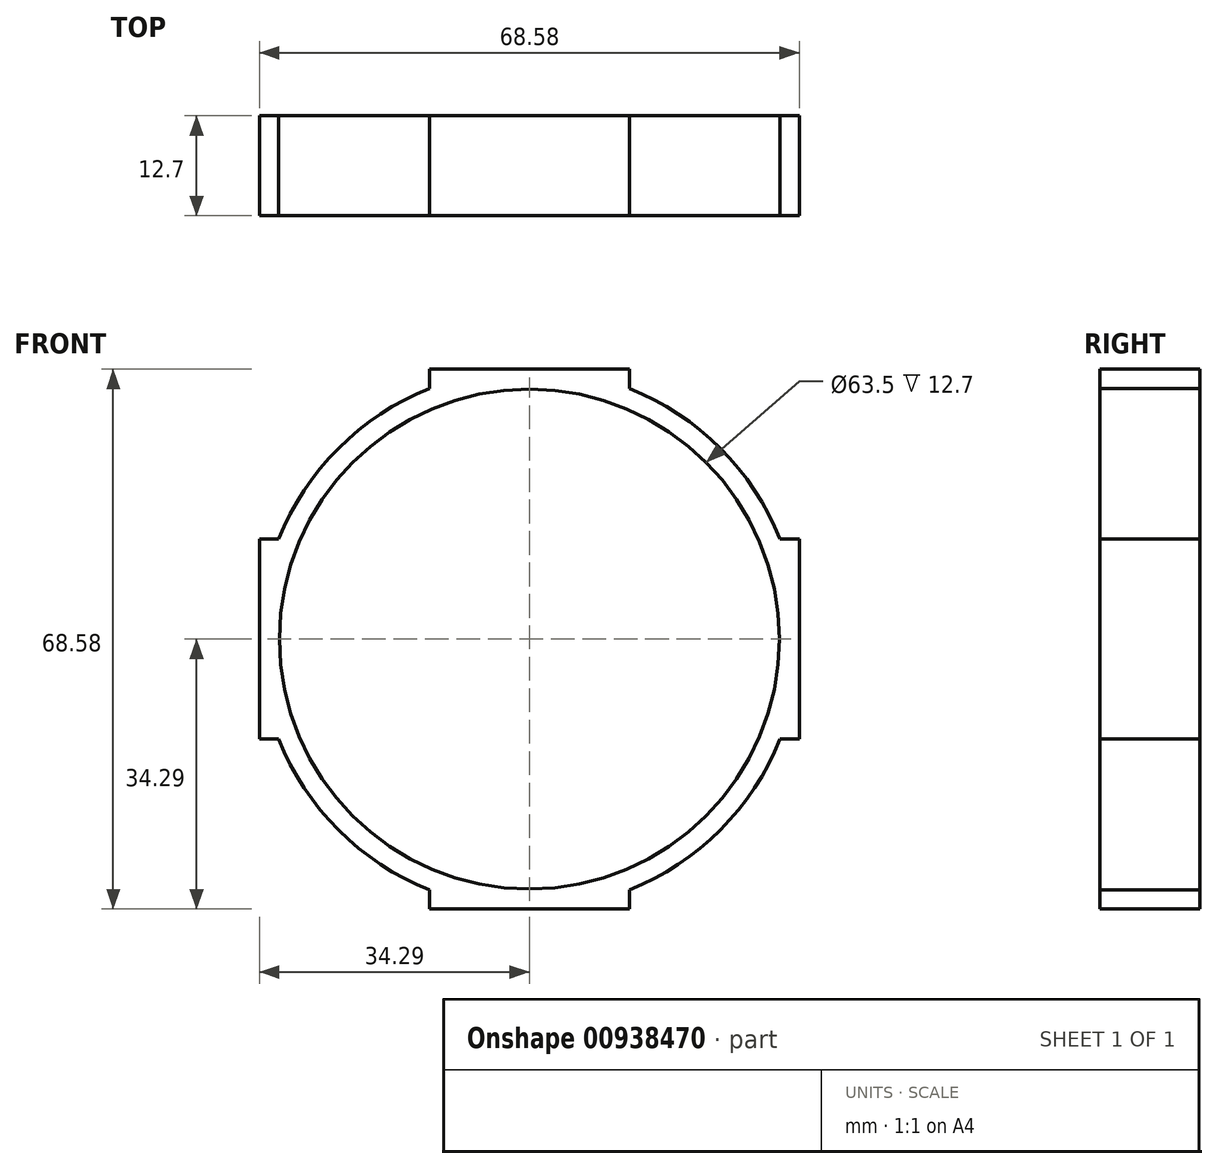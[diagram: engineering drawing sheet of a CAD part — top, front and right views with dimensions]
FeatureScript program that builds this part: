
annotation { "Feature Type Name" : "Feature", "Feature Type Description" : "" }
export const myFeature = defineFeature(function(context is Context, id is Id, definition is map)
    precondition{}
    {
        {
            var Q0;
            Q0=qCreatedBy(makeId("Front.planeOp"),FACE);
            var sketch = newSketch(context, id + "F0", { "sketchPlane" : qUnion([Q0])});
            skCircle(sketch, "E0", {"center": v(0, 0) * mm, "radius": 34.3 * mm});
            skCircle(sketch, "E1", {"center": v(0, 0) * mm, "radius": 31.75 * mm});
            skLineSegment(sketch, "E2", {"start": v(-12.7, 34.3) * mm, "end": v(12.7, 34.3) * mm});
            skLineSegment(sketch, "E3", {"start": v(12.7, 34.3) * mm, "end": v(12.7, 31.85) * mm});
            skLineSegment(sketch, "E4", {"start": v(-12.7, 34.3) * mm, "end": v(-12.7, 31.85) * mm});
            skLineSegment(sketch, "E5.MirrorCS", {"start": v(12.7, -34.3) * mm, "end": v(12.7, -31.85) * mm});
            skLineSegment(sketch, "E6.MirrorCS", {"start": v(-12.7, -34.3) * mm, "end": v(12.7, -34.3) * mm});
            skLineSegment(sketch, "E7.MirrorCS", {"start": v(-12.7, -34.3) * mm, "end": v(-12.7, -31.85) * mm});
            skLineSegment(sketch, "E8", {"start": v(-31.85, -12.7) * mm, "end": v(-34.3, -12.7) * mm});
            skLineSegment(sketch, "E9", {"start": v(-34.3, -12.7) * mm, "end": v(-34.3, 12.7) * mm});
            skLineSegment(sketch, "E10", {"start": v(-34.3, 12.7) * mm, "end": v(-31.85, 12.7) * mm});
            skLineSegment(sketch, "E11.MirrorCS", {"start": v(34.3, 12.7) * mm, "end": v(31.85, 12.7) * mm});
            skLineSegment(sketch, "E12.MirrorCS", {"start": v(34.3, -12.7) * mm, "end": v(34.3, 12.7) * mm});
            skLineSegment(sketch, "E13.MirrorCS", {"start": v(31.85, -12.7) * mm, "end": v(34.3, -12.7) * mm});
            skSolve(sketch);
        }
        {
            var Q0;
            Q0=makeQuery(id+"F0.imprint","IMPRINT",FACE,{"disambiguationData":[TD([[makeQuery(id+"F0.imprint","IMPRINT",EDGE,{"derivedFrom":sQuery(id+"F0.wireOp",EDGE,"E0")}),1.0]])]});
            var Q1;
            {var subQ0=sQuery(id+"F0.wireOp",EDGE,"E10");Q1=makeQuery(id+"F0.imprint","IMPRINT",FACE,{"disambiguationData":[TD([[makeQuery(id+"F0.imprint","IMPRINT",EDGE,{"derivedFrom":subQ0}),-1.0]])]});}
            var Q2;
            {var subQ0=sQuery(id+"F0.wireOp",EDGE,"E8");Q2=makeQuery(id+"F0.imprint","IMPRINT",FACE,{"disambiguationData":[TD([[makeQuery(id+"F0.imprint","IMPRINT",EDGE,{"derivedFrom":subQ0}),-1.0]])]});}
            var Q3;
            {var subQ0=sQuery(id+"F0.wireOp",EDGE,"E4");Q3=makeQuery(id+"F0.imprint","IMPRINT",FACE,{"disambiguationData":[TD([[makeQuery(id+"F0.imprint","IMPRINT",EDGE,{"derivedFrom":subQ0}),1.0]])]});}
            var Q4;
            {var subQ0=sQuery(id+"F0.wireOp",EDGE,"E3");Q4=makeQuery(id+"F0.imprint","IMPRINT",FACE,{"disambiguationData":[TD([[makeQuery(id+"F0.imprint","IMPRINT",EDGE,{"derivedFrom":subQ0}),-1.0]])]});}
            var Q5;
            {var subQ0=sQuery(id+"F0.wireOp",EDGE,"E11.MirrorCS");Q5=makeQuery(id+"F0.imprint","IMPRINT",FACE,{"disambiguationData":[TD([[makeQuery(id+"F0.imprint","IMPRINT",EDGE,{"derivedFrom":subQ0}),1.0]])]});}
            var Q6;
            {var subQ0=sQuery(id+"F0.wireOp",EDGE,"E13.MirrorCS");Q6=makeQuery(id+"F0.imprint","IMPRINT",FACE,{"disambiguationData":[TD([[makeQuery(id+"F0.imprint","IMPRINT",EDGE,{"derivedFrom":subQ0}),1.0]])]});}
            var Q7;
            {var subQ0=sQuery(id+"F0.wireOp",EDGE,"E5.MirrorCS");Q7=makeQuery(id+"F0.imprint","IMPRINT",FACE,{"disambiguationData":[TD([[makeQuery(id+"F0.imprint","IMPRINT",EDGE,{"derivedFrom":subQ0}),1.0]])]});}
            var Q8;
            {var subQ0=sQuery(id+"F0.wireOp",EDGE,"E7.MirrorCS");Q8=makeQuery(id+"F0.imprint","IMPRINT",FACE,{"disambiguationData":[TD([[makeQuery(id+"F0.imprint","IMPRINT",EDGE,{"derivedFrom":subQ0}),-1.0]])]});}
            extrude(context, id + "F1", {"entities" : qUnion([Q0, Q1, Q2, Q3, Q4, Q5, Q6, Q7, Q8]), "endBound" : BoundingType.SYMMETRIC, "depth" : 12.7 * mm, "offsetDistance" : 25.4 * mm});
        }
    });
